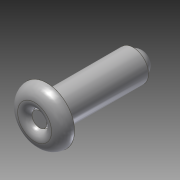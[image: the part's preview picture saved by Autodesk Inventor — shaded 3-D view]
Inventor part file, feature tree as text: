
AUTODESK INVENTOR PART (.ipt)
format: ipt  version: 2014 SP1 (Build 180222100, 222)  size: 146,944 bytes
history: native  units: in
note: dims shown in document units (in); Inventor stores cm internally (conversion verified against a paired STEP export)
features: extrude x3, sketch x2, fillet x1, revolve x1, boolean_combine x1
ambient origin geometry x8: Origin, YZ Plane, XZ Plane, XY Plane, X Axis, Y Axis, Z Axis, Center Point
bodies: Solid1 (feature_tree), Solid2 (feature_tree)
feature tree (8):
  sketch  "Sketch1"  dims[d0=0.125in d1=0.225in]
  extrude  "Extrusion1"  Depth=0.225in
  extrude  "Extrusion2"  Depth=0.35in TaperAngle=0.0deg
  fillet  "Fillet1"  Radius=0.05in
  sketch  "Sketch2"  dims[d2=0.07in d3=0.35in d4=0.0in d5=0.05in d6=0.0in d7=0.05in d8=0.03in d9=0.1in d10=90.0deg d11=0.06in d12=0.38in d13=0.0in]
  revolve  "Revolution1"  [1 undecoded]
  extrude  "Extrusion3"  Depth=0.03in
  boolean_combine  "Combine1"
note: 1 required parameter value undecoded (feature->parameter linkage not recoverable at this tier; creation-order binding heuristic only, values carry confidence <= 0.55)
